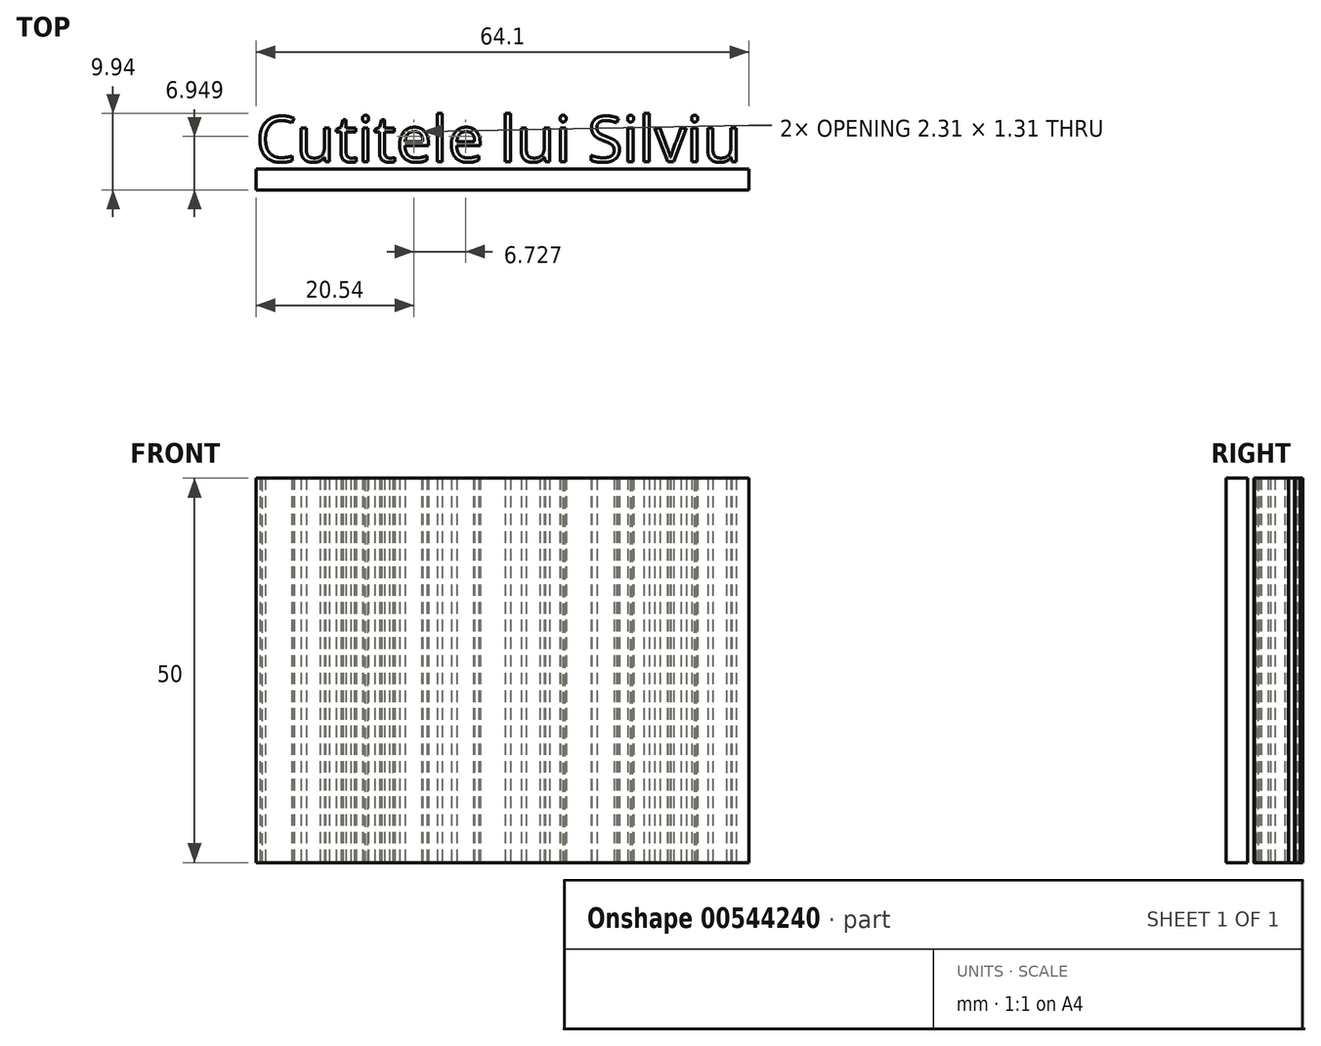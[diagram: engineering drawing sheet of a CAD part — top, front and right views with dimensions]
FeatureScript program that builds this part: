
annotation { "Feature Type Name" : "Feature", "Feature Type Description" : "" }
export const myFeature = defineFeature(function(context is Context, id is Id, definition is map)
    precondition{}
    {
        {
            var Q0;
            Q0=qCreatedBy(makeId("Top.planeOp"),FACE);
            var sketch = newSketch(context, id + "F0", { "sketchPlane" : qUnion([Q0])});
            skText(sketch, "E0", { "text": "Cutitele lui Silviu", "fontName": "OpenSans-Regular.ttf"});
            const initialGuessF0  = {"E0": [-0.07005, 0.0554, 1, 0, 0.00595]};
            skSetInitialGuess(sketch, initialGuessF0);
            skSolve(sketch);
        }
        {
            var Q0;
            Q0 = qSketchRegion(id + "F0", true);
            extrude(context, id + "F1", {"entities" : qUnion([Q0]), "depth" : 50 * mm, "offsetDistance" : 25 * mm});
        }
        {
            var Q0;
            Q0=qCreatedBy(makeId("Top.planeOp"),FACE);
            var sketch = newSketch(context, id + "F2", { "sketchPlane" : qUnion([Q0])});
            skLineSegment(sketch, "E1.bottom", {"start": v(-70.05, 54.48) * mm, "end": v(-5.95, 54.48) * mm});
            skLineSegment(sketch, "E1.top", {"start": v(-70.05, 51.74) * mm, "end": v(-5.95, 51.74) * mm});
            skLineSegment(sketch, "E1.left", {"start": v(-70.05, 54.48) * mm, "end": v(-70.05, 51.74) * mm});
            skLineSegment(sketch, "E1.right", {"start": v(-5.95, 54.48) * mm, "end": v(-5.95, 51.74) * mm});
            skSolve(sketch);
        }
        {
            var Q0;
            Q0 = qSketchRegion(id + "F2", true);
            extrude(context, id + "F3", {"entities" : qUnion([Q0]), "depth" : 50 * mm, "offsetDistance" : 25 * mm});
        }
    });
